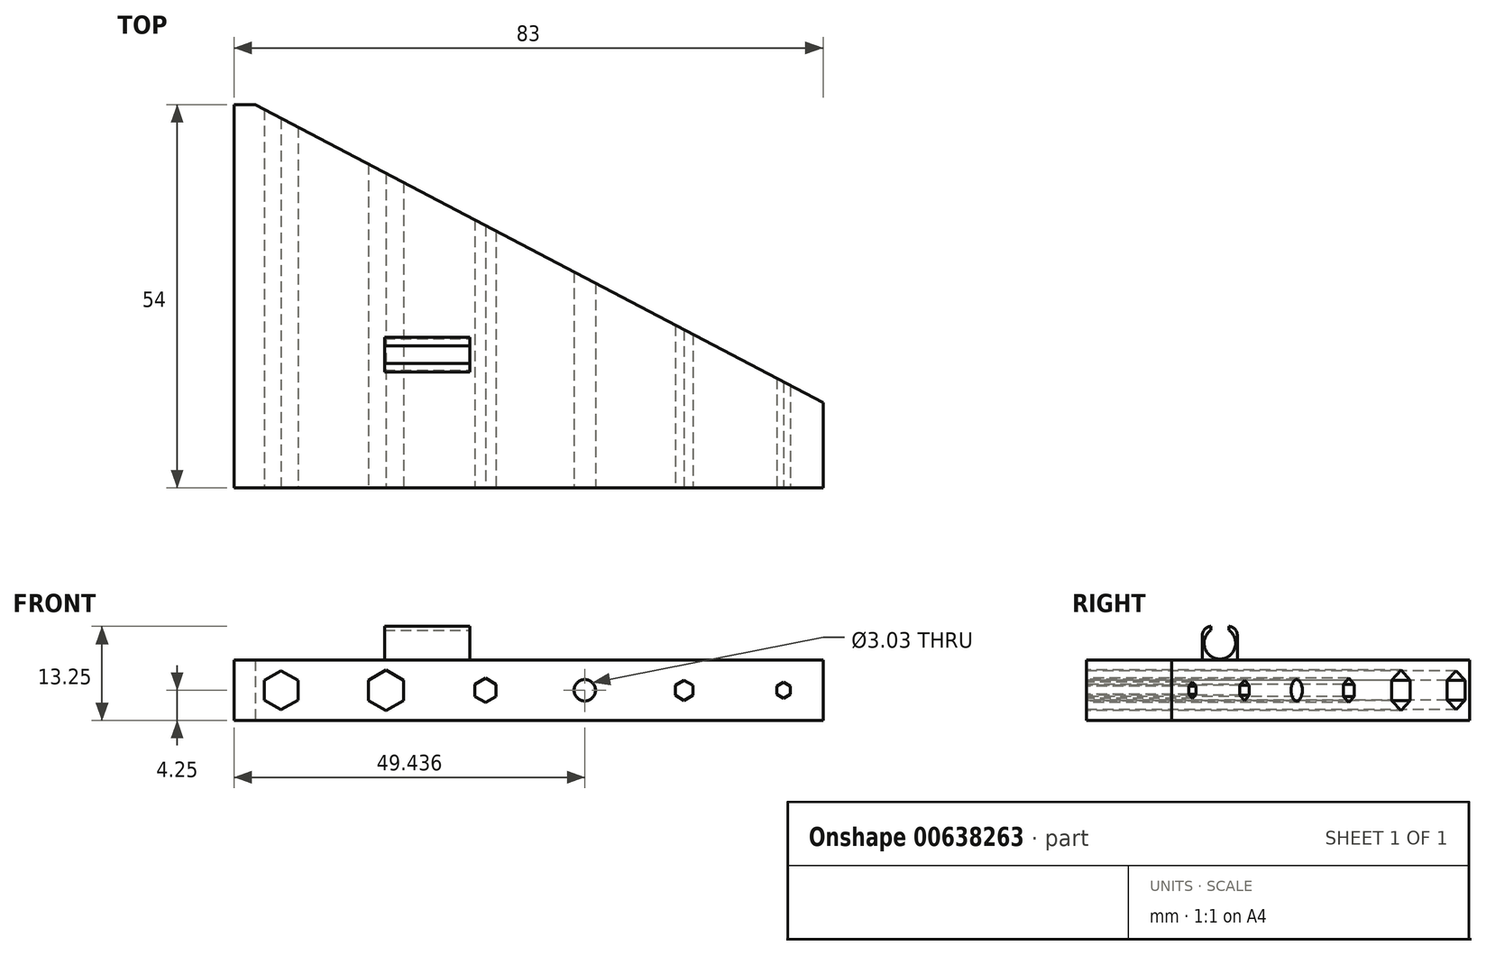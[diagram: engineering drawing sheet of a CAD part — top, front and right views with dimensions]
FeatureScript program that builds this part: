
annotation { "Feature Type Name" : "Feature", "Feature Type Description" : "" }
export const myFeature = defineFeature(function(context is Context, id is Id, definition is map)
    precondition{}
    {
        {
            var Q0;
            Q0=qCreatedBy(makeId("Top.planeOp"),FACE);
            var sketch = newSketch(context, id + "F0", { "sketchPlane" : qUnion([Q0])});
            skLineSegment(sketch, "E0", {"start": v(0, 0) * mm, "end": v(83, 0) * mm});
            skLineSegment(sketch, "E1", {"start": v(83, 0) * mm, "end": v(83, 12) * mm});
            skLineSegment(sketch, "E2", {"start": v(0, 0) * mm, "end": v(0, 54) * mm});
            skLineSegment(sketch, "E3", {"start": v(0, 54) * mm, "end": v(3, 54) * mm});
            skLineSegment(sketch, "E4", {"start": v(3, 54) * mm, "end": v(83, 12) * mm});
            skSolve(sketch);
        }
        {
            var Q0;
            Q0=makeQuery(id+"F0.imprint","IMPRINT",FACE,{"disambiguationData":[TD([[makeQuery(id+"F0.imprint","IMPRINT",EDGE,{"derivedFrom":sQuery(id+"F0.wireOp",EDGE,"E0")}),1.0]])]});
            extrude(context, id + "F1", {"entities" : qUnion([Q0]), "depth" : 8.5 * mm, "offsetDistance" : 25 * mm});
        }
        {
            var Q0;
            Q0=makeQuery(id+"F1.opExtrude","SWEPT_FACE",FACE,{"disambiguationData":[OSD([sQuery(id+"F0.wireOp",EDGE,"E0")])]});
            var sketch = newSketch(context, id + "F2", { "sketchPlane" : qUnion([Q0])});
            skLineSegment(sketch, "E5", {"start": v(3, 8.5) * mm, "end": v(3, 0) * mm});
            skLineSegment(sketch, "E6", {"start": v(3, 4.25) * mm, "end": v(21.44, 4.25) * mm});
            skCircle(sketch, "E7.cCircle", {"center": v(6.64, 4.25) * mm, "radius": 2.37 * mm, "construction": true});
            skLineSegment(sketch, "E7.0", {"start": v(9.02, 5.62) * mm, "end": v(9.02, 2.88) * mm});
            skLineSegment(sketch, "E7.1", {"start": v(9.02, 2.88) * mm, "end": v(6.64, 1.5) * mm});
            skLineSegment(sketch, "E7.2", {"start": v(6.64, 1.5) * mm, "end": v(4.27, 2.88) * mm});
            skLineSegment(sketch, "E7.3", {"start": v(4.27, 2.88) * mm, "end": v(4.27, 5.62) * mm});
            skLineSegment(sketch, "E7.4", {"start": v(4.27, 5.62) * mm, "end": v(6.64, 7) * mm});
            skLineSegment(sketch, "E7.5", {"start": v(6.64, 7) * mm, "end": v(9.02, 5.62) * mm});
            skPoint(sketch, "E7.0.midPoint", {"position": v(9.02, 4.25) * mm});
            skPoint(sketch, "E8.orphan", {"position": v(4.27, 4.25) * mm});
            skLineSegment(sketch, "E9", {"start": v(9.02, 4.25) * mm, "end": v(21.44, 4.25) * mm});
            skPoint(sketch, "E10.orphan", {"position": v(83, 4.25) * mm});
            skLineSegment(sketch, "E11", {"start": v(21.44, 4.25) * mm, "end": v(23.91, 4.25) * mm});
            skCircle(sketch, "E12.cCircle", {"center": v(21.44, 4.25) * mm, "radius": 2.48 * mm, "construction": true});
            skLineSegment(sketch, "E12.0", {"start": v(23.91, 5.68) * mm, "end": v(23.91, 2.82) * mm});
            skLineSegment(sketch, "E12.1", {"start": v(23.91, 2.82) * mm, "end": v(21.44, 1.4) * mm});
            skLineSegment(sketch, "E12.2", {"start": v(21.44, 1.4) * mm, "end": v(18.96, 2.82) * mm});
            skLineSegment(sketch, "E12.3", {"start": v(18.96, 2.82) * mm, "end": v(18.96, 5.68) * mm});
            skLineSegment(sketch, "E12.4", {"start": v(18.96, 5.68) * mm, "end": v(21.44, 7.1) * mm});
            skLineSegment(sketch, "E12.5", {"start": v(21.44, 7.1) * mm, "end": v(23.91, 5.68) * mm});
            skPoint(sketch, "E12.0.midPoint", {"position": v(23.91, 4.25) * mm});
            skLineSegment(sketch, "E13", {"start": v(21.44, 4.25) * mm, "end": v(35.44, 4.25) * mm});
            skLineSegment(sketch, "E14", {"start": v(35.44, 4.25) * mm, "end": v(36.92, 4.25) * mm});
            skCircle(sketch, "E15.cCircle", {"center": v(35.44, 4.25) * mm, "radius": 1.48 * mm, "construction": true});
            skLineSegment(sketch, "E15.0", {"start": v(36.92, 5.1) * mm, "end": v(36.92, 3.4) * mm});
            skLineSegment(sketch, "E15.1", {"start": v(36.92, 3.4) * mm, "end": v(35.44, 2.54) * mm});
            skLineSegment(sketch, "E15.2", {"start": v(35.44, 2.54) * mm, "end": v(33.96, 3.4) * mm});
            skLineSegment(sketch, "E15.3", {"start": v(33.96, 3.4) * mm, "end": v(33.96, 5.1) * mm});
            skLineSegment(sketch, "E15.4", {"start": v(33.96, 5.1) * mm, "end": v(35.44, 5.96) * mm});
            skLineSegment(sketch, "E15.5", {"start": v(35.44, 5.96) * mm, "end": v(36.92, 5.1) * mm});
            skPoint(sketch, "E15.0.midPoint", {"position": v(36.92, 4.25) * mm});
            skLineSegment(sketch, "E16", {"start": v(35.44, 4.25) * mm, "end": v(49.44, 4.25) * mm});
            skLineSegment(sketch, "E17", {"start": v(49.44, 4.25) * mm, "end": v(50.95, 4.25) * mm});
            skCircle(sketch, "E18", {"center": v(49.44, 4.25) * mm, "radius": 1.52 * mm});
            skLineSegment(sketch, "E19", {"start": v(49.44, 4.25) * mm, "end": v(63.44, 4.25) * mm});
            skLineSegment(sketch, "E20", {"start": v(63.44, 4.25) * mm, "end": v(64.67, 4.25) * mm});
            skCircle(sketch, "E21.cCircle", {"center": v(63.44, 4.25) * mm, "radius": 1.23 * mm, "construction": true});
            skLineSegment(sketch, "E21.0", {"start": v(64.67, 4.96) * mm, "end": v(64.67, 3.54) * mm});
            skLineSegment(sketch, "E21.1", {"start": v(64.67, 3.54) * mm, "end": v(63.44, 2.82) * mm});
            skLineSegment(sketch, "E21.2", {"start": v(63.44, 2.82) * mm, "end": v(62.2, 3.54) * mm});
            skLineSegment(sketch, "E21.3", {"start": v(62.2, 3.54) * mm, "end": v(62.2, 4.96) * mm});
            skLineSegment(sketch, "E21.4", {"start": v(62.2, 4.96) * mm, "end": v(63.44, 5.68) * mm});
            skLineSegment(sketch, "E21.5", {"start": v(63.44, 5.68) * mm, "end": v(64.67, 4.96) * mm});
            skPoint(sketch, "E21.0.midPoint", {"position": v(64.67, 4.25) * mm});
            skLineSegment(sketch, "E22", {"start": v(63.44, 4.25) * mm, "end": v(77.44, 4.25) * mm});
            skLineSegment(sketch, "E23", {"start": v(77.44, 4.25) * mm, "end": v(78.42, 4.25) * mm});
            skCircle(sketch, "E24.cCircle", {"center": v(77.44, 4.25) * mm, "radius": 0.98 * mm, "construction": true});
            skLineSegment(sketch, "E24.0", {"start": v(78.42, 4.82) * mm, "end": v(78.42, 3.68) * mm});
            skLineSegment(sketch, "E24.1", {"start": v(78.42, 3.68) * mm, "end": v(77.44, 3.12) * mm});
            skLineSegment(sketch, "E24.2", {"start": v(77.44, 3.12) * mm, "end": v(76.46, 3.68) * mm});
            skLineSegment(sketch, "E24.3", {"start": v(76.46, 3.68) * mm, "end": v(76.46, 4.82) * mm});
            skLineSegment(sketch, "E24.4", {"start": v(76.46, 4.82) * mm, "end": v(77.44, 5.38) * mm});
            skLineSegment(sketch, "E24.5", {"start": v(77.44, 5.38) * mm, "end": v(78.42, 4.82) * mm});
            skPoint(sketch, "E24.0.midPoint", {"position": v(78.42, 4.25) * mm});
            skSolve(sketch);
        }
        {
            var Q0;
            {var subQ1=sQuery(id+"F2.wireOp",EDGE,"E7.1");Q0=makeQuery(id+"F2.imprint","IMPRINT",FACE,{"disambiguationData":[TD([[makeQuery(id+"F2.imprint","IMPRINT",EDGE,{"derivedFrom":subQ1}),-1.0]])]});}
            var Q1;
            {var subQ0=sQuery(id+"F2.wireOp",EDGE,"E7.4");Q1=makeQuery(id+"F2.imprint","IMPRINT",FACE,{"disambiguationData":[TD([[makeQuery(id+"F2.imprint","IMPRINT",EDGE,{"derivedFrom":subQ0}),-1.0]])]});}
            var Q2;
            {var subQ0=sQuery(id+"F2.wireOp",EDGE,"E12.4");Q2=makeQuery(id+"F2.imprint","IMPRINT",FACE,{"disambiguationData":[TD([[makeQuery(id+"F2.imprint","IMPRINT",EDGE,{"derivedFrom":subQ0}),-1.0]])]});}
            var Q3;
            {var subQ1=sQuery(id+"F2.wireOp",EDGE,"E12.1");Q3=makeQuery(id+"F2.imprint","IMPRINT",FACE,{"disambiguationData":[TD([[makeQuery(id+"F2.imprint","IMPRINT",EDGE,{"derivedFrom":subQ1}),-1.0]])]});}
            var Q4;
            {var subQ0=sQuery(id+"F2.wireOp",EDGE,"E15.4");Q4=makeQuery(id+"F2.imprint","IMPRINT",FACE,{"disambiguationData":[TD([[makeQuery(id+"F2.imprint","IMPRINT",EDGE,{"derivedFrom":subQ0}),-1.0]])]});}
            var Q5;
            {var subQ1=sQuery(id+"F2.wireOp",EDGE,"E15.1");Q5=makeQuery(id+"F2.imprint","IMPRINT",FACE,{"disambiguationData":[TD([[makeQuery(id+"F2.imprint","IMPRINT",EDGE,{"derivedFrom":subQ1}),-1.0]])]});}
            var Q6;
            {var subQ0=sQuery(id+"F2.wireOp",EDGE,"E19");var subQ1=sQuery(id+"F2.wireOp",EDGE,"E16");var subQ2=makeQuery(id+"F2.imprint","INTERSECT",VERTEX,{"derivedFrom":[subQ1,subQ0]});Q6=makeQuery(id+"F2.imprint","IMPRINT",FACE,{"disambiguationData":[TD([[makeQuery(id+"F2.imprint","IMPRINT",EDGE,{"disambiguationData":[TD([[subQ2,1.0]])],"derivedFrom":subQ1}),-1.0]])]});}
            var Q7;
            {var subQ0=sQuery(id+"F2.wireOp",EDGE,"E19");var subQ1=sQuery(id+"F2.wireOp",EDGE,"E16");var subQ2=makeQuery(id+"F2.imprint","INTERSECT",VERTEX,{"derivedFrom":[subQ1,subQ0]});Q7=makeQuery(id+"F2.imprint","IMPRINT",FACE,{"disambiguationData":[TD([[makeQuery(id+"F2.imprint","IMPRINT",EDGE,{"disambiguationData":[TD([[subQ2,1.0]])],"derivedFrom":subQ1}),1.0]])]});}
            var Q8;
            {var subQ0=sQuery(id+"F2.wireOp",EDGE,"E21.4");Q8=makeQuery(id+"F2.imprint","IMPRINT",FACE,{"disambiguationData":[TD([[makeQuery(id+"F2.imprint","IMPRINT",EDGE,{"derivedFrom":subQ0}),-1.0]])]});}
            var Q9;
            {var subQ1=sQuery(id+"F2.wireOp",EDGE,"E21.1");Q9=makeQuery(id+"F2.imprint","IMPRINT",FACE,{"disambiguationData":[TD([[makeQuery(id+"F2.imprint","IMPRINT",EDGE,{"derivedFrom":subQ1}),-1.0]])]});}
            var Q10;
            {var subQ2=sQuery(id+"F2.wireOp",EDGE,"E23");Q10=makeQuery(id+"F2.imprint","IMPRINT",FACE,{"disambiguationData":[TD([[makeQuery(id+"F2.imprint","IMPRINT",EDGE,{"derivedFrom":subQ2}),-1.0]])]});}
            var Q11;
            {var subQ5=sQuery(id+"F2.wireOp",EDGE,"E23");Q11=makeQuery(id+"F2.imprint","IMPRINT",FACE,{"disambiguationData":[TD([[makeQuery(id+"F2.imprint","IMPRINT",EDGE,{"derivedFrom":subQ5}),1.0]])]});}
            extrude(context, id + "F3", {"entities" : qUnion([Q0, Q1, Q2, Q3, Q4, Q5, Q6, Q7, Q8, Q9, Q10, Q11]), "operationType" : NewBodyOperationType.REMOVE, "oppositeDirection" : true, "depth" : 68.6 * mm, "offsetDistance" : 25 * mm});
        }
        {
            var Q0;
            Q0=makeQuery(id+"F1.opExtrude","CAP_FACE",FACE,{"disambiguationData":[OSD([sQuery(id+"F0.wireOp",EDGE,"E0"),sQuery(id+"F0.wireOp",EDGE,"E1"),sQuery(id+"F0.wireOp",EDGE,"E2"),sQuery(id+"F0.wireOp",EDGE,"E3"),sQuery(id+"F0.wireOp",EDGE,"E4")])],"isStart":false});
            var sketch = newSketch(context, id + "F4", { "sketchPlane" : qUnion([Q0])});
            skLineSegment(sketch, "E25", {"start": v(27.21, 18.8) * mm, "end": v(21.21, 18.8) * mm});
            skLineSegment(sketch, "E26", {"start": v(27.21, 18.8) * mm, "end": v(33.21, 18.8) * mm});
            skLineSegment(sketch, "E27", {"start": v(27.21, 18.8) * mm, "end": v(27.21, 21.25) * mm});
            skLineSegment(sketch, "E28", {"start": v(27.21, 18.8) * mm, "end": v(27.21, 16.35) * mm});
            skLineSegment(sketch, "E29.bottom", {"start": v(21.21, 16.35) * mm, "end": v(33.21, 16.35) * mm});
            skLineSegment(sketch, "E29.top", {"start": v(21.21, 21.25) * mm, "end": v(33.21, 21.25) * mm});
            skLineSegment(sketch, "E29.left", {"start": v(21.21, 16.35) * mm, "end": v(21.21, 21.25) * mm});
            skLineSegment(sketch, "E29.right", {"start": v(33.21, 16.35) * mm, "end": v(33.21, 21.25) * mm});
            skSolve(sketch);
        }
        {
            var Q0;
            {var subQ0=sQuery(id+"F4.wireOp",EDGE,"E26");Q0=makeQuery(id+"F4.imprint","IMPRINT",FACE,{"disambiguationData":[TD([[makeQuery(id+"F4.imprint","IMPRINT",EDGE,{"derivedFrom":subQ0}),-1.0]])]});}
            var Q1;
            {var subQ0=sQuery(id+"F4.wireOp",EDGE,"E25");Q1=makeQuery(id+"F4.imprint","IMPRINT",FACE,{"disambiguationData":[TD([[makeQuery(id+"F4.imprint","IMPRINT",EDGE,{"derivedFrom":subQ0}),-1.0]])]});}
            var Q2;
            {var subQ0=sQuery(id+"F4.wireOp",EDGE,"E25");Q2=makeQuery(id+"F4.imprint","IMPRINT",FACE,{"disambiguationData":[TD([[makeQuery(id+"F4.imprint","IMPRINT",EDGE,{"derivedFrom":subQ0}),1.0]])]});}
            var Q3;
            {var subQ0=sQuery(id+"F4.wireOp",EDGE,"E26");Q3=makeQuery(id+"F4.imprint","IMPRINT",FACE,{"disambiguationData":[TD([[makeQuery(id+"F4.imprint","IMPRINT",EDGE,{"derivedFrom":subQ0}),1.0]])]});}
            extrude(context, id + "F5", {"entities" : qUnion([Q0, Q1, Q2, Q3]), "operationType" : NewBodyOperationType.ADD, "depth" : 4.75 * mm, "offsetDistance" : 25 * mm});
        }
        {
            var Q0;
            Q0=makeQuery(id+"F5.opExtrude","SWEPT_FACE",FACE,{"disambiguationData":[OSD([sQuery(id+"F4.wireOp",EDGE,"E29.right")])]});
            var sketch = newSketch(context, id + "F6", { "sketchPlane" : qUnion([Q0])});
            skCircle(sketch, "E30", {"center": v(18.8, 10.88) * mm, "radius": 2.23 * mm});
            skPoint(sketch, "E30.centerSnap0", {"position": v(18.8, 13.25) * mm});
            skPoint(sketch, "E30.centerSnap1", {"position": v(16.35, 10.88) * mm});
            skSolve(sketch);
        }
        {
            var Q0;
            Q0=makeQuery(id+"F6.imprint","IMPRINT",FACE,{"disambiguationData":[TD([[makeQuery(id+"F6.imprint","IMPRINT",EDGE,{"derivedFrom":sQuery(id+"F6.wireOp",EDGE,"E30")}),1.0]])]});
            extrude(context, id + "F7", {"entities" : qUnion([Q0]), "operationType" : NewBodyOperationType.REMOVE, "oppositeDirection" : true, "depth" : 25 * mm, "offsetDistance" : 25 * mm});
        }
        {
            var Q0;
            Q0=makeQuery(id+"F5.opExtrude","CAP_EDGE",EDGE,{"disambiguationData":[OSD([sQuery(id+"F4.wireOp",EDGE,"E29.top")])],"isStart":false});
            fillet(context, id + "F8", {"entities" : qUnion([Q0]), "radius" : 1.2 * mm, "tangentPropagation" : true, "allowEdgeOverflow" : false});
        }
        {
            var Q0;
            Q0=makeQuery(id+"F5.opExtrude","CAP_EDGE",EDGE,{"disambiguationData":[OSD([sQuery(id+"F4.wireOp",EDGE,"E29.bottom")])],"isStart":false});
            fillet(context, id + "F9", {"entities" : qUnion([Q0]), "radius" : 1.2 * mm, "tangentPropagation" : true, "allowEdgeOverflow" : false});
        }
        {
            var Q0;
            Q0=makeQuery(id+"F5.opExtrude","CAP_FACE",FACE,{"disambiguationData":[OSD([sQuery(id+"F4.wireOp",EDGE,"E29.bottom"),sQuery(id+"F4.wireOp",EDGE,"E29.top"),sQuery(id+"F4.wireOp",EDGE,"E29.left"),sQuery(id+"F4.wireOp",EDGE,"E29.right")])],"isStart":false});
            extrude(context, id + "F10", {"entities" : qUnion([Q0]), "operationType" : NewBodyOperationType.REMOVE, "oppositeDirection" : true, "depth" : 3 * mm, "offsetDistance" : 25 * mm});
        }
    });
